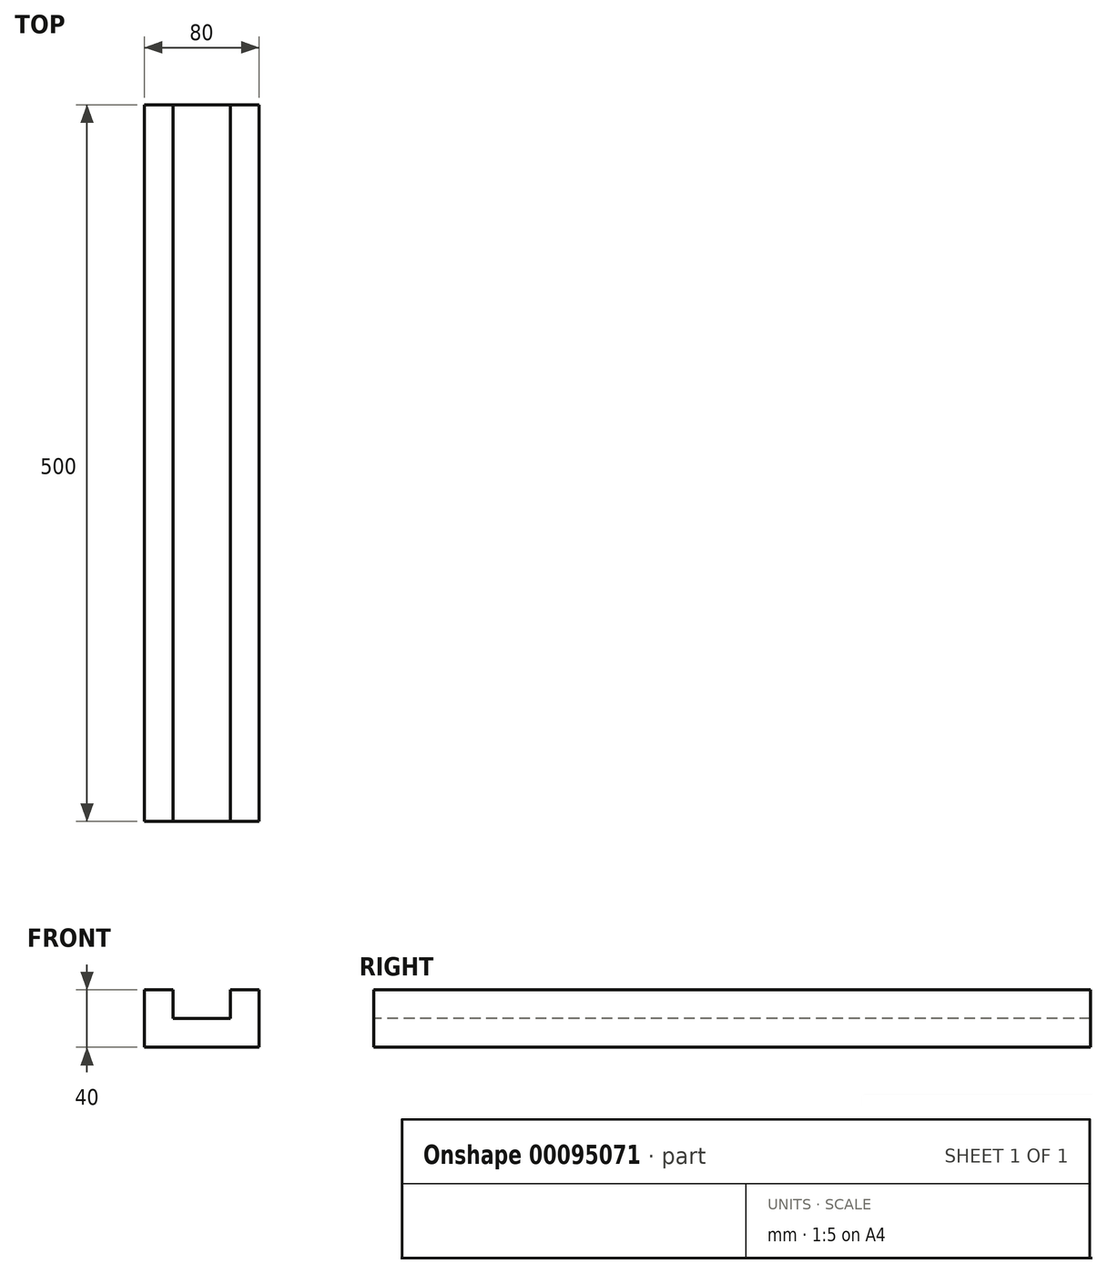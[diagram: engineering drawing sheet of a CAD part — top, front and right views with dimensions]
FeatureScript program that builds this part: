
annotation { "Feature Type Name" : "Feature", "Feature Type Description" : "" }
export const myFeature = defineFeature(function(context is Context, id is Id, definition is map)
    precondition{}
    {
        {
            var Q0;
            Q0=qCreatedBy(makeId("Top.planeOp"),FACE);
            var sketch = newSketch(context, id + "F0", { "sketchPlane" : qUnion([Q0])});
            skLineSegment(sketch, "E0.bottom", {"start": v(-40, 250) * mm, "end": v(40, 250) * mm});
            skLineSegment(sketch, "E0.top", {"start": v(-40, -250) * mm, "end": v(40, -250) * mm});
            skLineSegment(sketch, "E0.left", {"start": v(-40, 250) * mm, "end": v(-40, -250) * mm});
            skLineSegment(sketch, "E0.right", {"start": v(40, 250) * mm, "end": v(40, -250) * mm});
            skLineSegment(sketch, "E1", {"start": v(0, 250) * mm, "end": v(0, -250) * mm, "construction": true});
            skLineSegment(sketch, "E2", {"start": v(-40, 0) * mm, "end": v(40, 0) * mm, "construction": true});
            skSolve(sketch);
        }
        {
            var Q0;
            Q0=makeQuery(id+"F0.imprint","IMPRINT",FACE,{"disambiguationData":[TD([[makeQuery(id+"F0.imprint","IMPRINT",EDGE,{"derivedFrom":sQuery(id+"F0.wireOp",EDGE,"E0.bottom")}),-1.0]])]});
            extrude(context, id + "F1", {"entities" : qUnion([Q0]), "depth" : 20 * mm});
        }
        {
            var Q0;
            Q0=makeQuery(id+"F1.opExtrude","CAP_FACE",FACE,{"disambiguationData":[OSD([sQuery(id+"F0.wireOp",EDGE,"E0.bottom"),sQuery(id+"F0.wireOp",EDGE,"E0.top"),sQuery(id+"F0.wireOp",EDGE,"E0.left"),sQuery(id+"F0.wireOp",EDGE,"E0.right")])],"isStart":false});
            var sketch = newSketch(context, id + "F2", { "sketchPlane" : qUnion([Q0])});
            skLineSegment(sketch, "E3.bottom", {"start": v(-40, 250) * mm, "end": v(-20, 250) * mm});
            skLineSegment(sketch, "E3.top", {"start": v(-40, -250) * mm, "end": v(-20, -250) * mm});
            skLineSegment(sketch, "E3.left", {"start": v(-40, 250) * mm, "end": v(-40, -250) * mm});
            skLineSegment(sketch, "E3.right", {"start": v(-20, 250) * mm, "end": v(-20, -250) * mm});
            skLineSegment(sketch, "E4.bottom", {"start": v(20, 250) * mm, "end": v(40, 250) * mm});
            skLineSegment(sketch, "E4.top", {"start": v(20, -250) * mm, "end": v(40, -250) * mm});
            skLineSegment(sketch, "E4.left", {"start": v(20, 250) * mm, "end": v(20, -250) * mm});
            skLineSegment(sketch, "E4.right", {"start": v(40, 250) * mm, "end": v(40, -250) * mm});
            skSolve(sketch);
        }
        {
            var Q0;
            Q0 = qSketchRegion(id + "F2", true);
            extrude(context, id + "F3", {"entities" : qUnion([Q0]), "operationType" : NewBodyOperationType.ADD, "depth" : 20 * mm});
        }
    });
